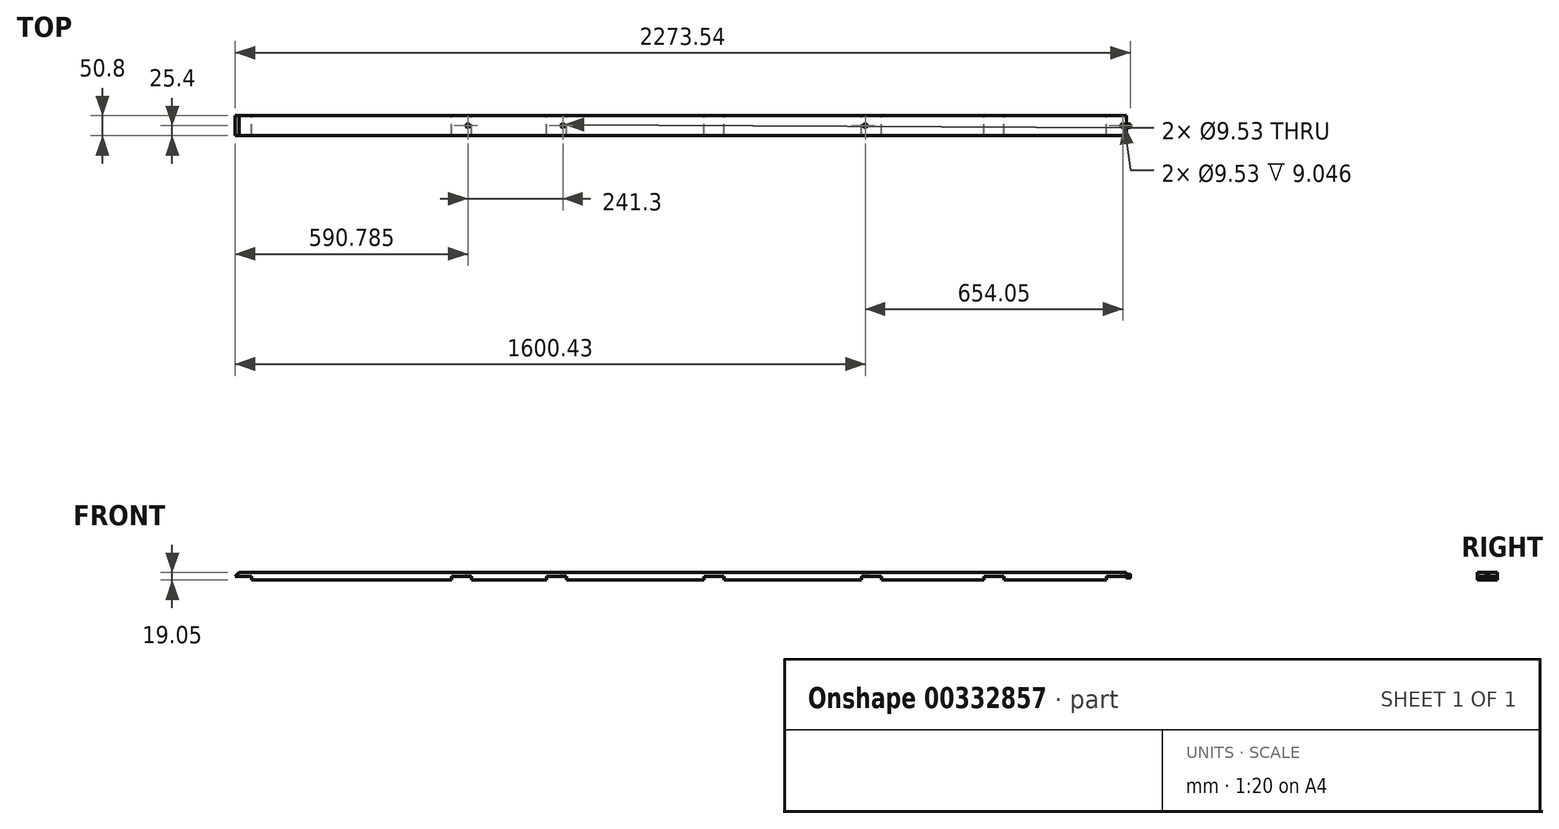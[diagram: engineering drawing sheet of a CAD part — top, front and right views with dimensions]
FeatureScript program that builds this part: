
annotation { "Feature Type Name" : "Feature", "Feature Type Description" : "" }
export const myFeature = defineFeature(function(context is Context, id is Id, definition is map)
    precondition{}
    {
        {
            var Q0;
            Q0=qCreatedBy(makeId("Front.planeOp"),FACE);
            var sketch = newSketch(context, id + "F0", { "sketchPlane" : qUnion([Q0])});
            skLineSegment(sketch, "E0.right", {"start": v(2273.3, 9.05) * mm, "end": v(2273.3, 18.57) * mm});
            skLineSegment(sketch, "E1", {"start": v(2273.3, 18.57) * mm, "end": v(18.57, 18.57) * mm});
            skPoint(sketch, "E2.left.start.orphan", {"position": v(-798.41, -3.82) * mm});
            skLineSegment(sketch, "E3.top", {"start": v(800.1, 9.52) * mm, "end": v(850.9, 9.52) * mm});
            skLineSegment(sketch, "E3.left", {"start": v(800.1, 0) * mm, "end": v(800.1, 9.52) * mm});
            skLineSegment(sketch, "E3.right", {"start": v(850.9, -0.48) * mm, "end": v(850.9, 9.52) * mm});
            skLineSegment(sketch, "E4.trimOffspring", {"start": v(850.9, -0.48) * mm, "end": v(1200.15, -0.48) * mm});
            skLineSegment(sketch, "E5.top", {"start": v(1600.2, 9.05) * mm, "end": v(1651, 9.05) * mm});
            skLineSegment(sketch, "E5.left", {"start": v(1600.2, -0.48) * mm, "end": v(1600.2, 9.05) * mm});
            skLineSegment(sketch, "E5.right", {"start": v(1651, -0.48) * mm, "end": v(1651, 9.05) * mm});
            skLineSegment(sketch, "E6.trimOffspring", {"start": v(1651, -0.48) * mm, "end": v(1911.35, -0.48) * mm});
            skLineSegment(sketch, "E7.top", {"start": v(2222.5, 9.05) * mm, "end": v(2273.3, 9.05) * mm});
            skLineSegment(sketch, "E7.left", {"start": v(2222.5, -0.48) * mm, "end": v(2222.5, 9.05) * mm});
            skPoint(sketch, "E8.orphan", {"position": v(2273.3, -0.48) * mm});
            skLineSegment(sketch, "E9", {"start": v(9.29, 9.29) * mm, "end": v(18.57, 18.57) * mm});
            skLineSegment(sketch, "E10.trimOffspring", {"start": v(50.8, 0) * mm, "end": v(558.8, 0) * mm});
            skLineSegment(sketch, "E11.top", {"start": v(9.29, 9.29) * mm, "end": v(50.8, 9.29) * mm});
            skLineSegment(sketch, "E11.right", {"start": v(50.8, 0) * mm, "end": v(50.8, 9.29) * mm});
            skPoint(sketch, "E12.orphan", {"position": v(0, 0) * mm});
            skLineSegment(sketch, "E13.bottom", {"start": v(609.6, 9.52) * mm, "end": v(558.8, 9.52) * mm});
            skLineSegment(sketch, "E13.left", {"start": v(609.6, 9.52) * mm, "end": v(609.6, 0) * mm});
            skLineSegment(sketch, "E13.right", {"start": v(558.8, 9.52) * mm, "end": v(558.8, 0) * mm});
            skLineSegment(sketch, "E14.trimOffspring", {"start": v(609.6, 0) * mm, "end": v(800.1, 0) * mm});
            skLineSegment(sketch, "E15.top", {"start": v(1962.15, 9.05) * mm, "end": v(1911.35, 9.05) * mm});
            skLineSegment(sketch, "E15.left", {"start": v(1962.15, -0.48) * mm, "end": v(1962.15, 9.05) * mm});
            skLineSegment(sketch, "E15.right", {"start": v(1911.35, -0.48) * mm, "end": v(1911.35, 9.05) * mm});
            skPoint(sketch, "E15.middle", {"position": v(1936.75, -0.48) * mm});
            skLineSegment(sketch, "E16.trimOffspring", {"start": v(1936.75, -0.48) * mm, "end": v(2222.5, -0.48) * mm});
            skPoint(sketch, "E17.orphan", {"position": v(1911.35, -10) * mm});
            skPoint(sketch, "E18.orphan", {"position": v(1962.15, -10) * mm});
            skLineSegment(sketch, "E19.top", {"start": v(1250.95, 9.05) * mm, "end": v(1200.15, 9.05) * mm});
            skLineSegment(sketch, "E19.left", {"start": v(1250.95, -0.48) * mm, "end": v(1250.95, 9.05) * mm});
            skLineSegment(sketch, "E19.right", {"start": v(1200.15, -0.48) * mm, "end": v(1200.15, 9.05) * mm});
            skPoint(sketch, "E19.middle", {"position": v(1225.55, -0.48) * mm});
            skPoint(sketch, "E19.bottom.end.orphan", {"position": v(1200.15, -10) * mm});
            skLineSegment(sketch, "E20.trimOffspring", {"start": v(1250.95, -0.48) * mm, "end": v(1600.2, -0.48) * mm});
            skPoint(sketch, "E21.orphan", {"position": v(1250.95, -10) * mm});
            skSolve(sketch);
        }
        {
            var Q0;
            Q0 = qSketchRegion(id + "F0", true);
            extrude(context, id + "F1", {"entities" : qUnion([Q0]), "depth" : 50.8 * mm});
        }
        {
            var Q0;
            Q0=qCreatedBy(makeId("Right.planeOp"),FACE);
            cPlane(context, id + "F2", {"entities" : qUnion([Q0]), "cplaneType" : CPlaneType.OFFSET, "offset" : 2273.3 * mm, "width" : 152.4 * mm, "height" : 152.4 * mm});
        }
        {
            var Q0;
            Q0=qCreatedBy(id+"F2.planeOp",FACE);
            var sketch = newSketch(context, id + "F3", { "sketchPlane" : qUnion([Q0])});
            skCircle(sketch, "E22", {"center": v(-25.4, 9.52) * mm, "radius": 4.76 * mm});
            skSolve(sketch);
        }
        {
            var Q0;
            Q0 = qSketchRegion(id + "F3", true);
            extrude(context, id + "F4", {"entities" : qUnion([Q0]), "operationType" : NewBodyOperationType.ADD, "depth" : 9.52 * mm});
        }
        {
            var Q0;
            Q0=qCreatedBy(makeId("Top.planeOp"),FACE);
            cPlane(context, id + "F5", {"entities" : qUnion([Q0]), "cplaneType" : CPlaneType.OFFSET, "offset" : 9.52 * mm, "width" : 152.4 * mm, "height" : 152.4 * mm});
        }
        {
            var Q0;
            Q0=qCreatedBy(id+"F5.planeOp",FACE);
            var sketch = newSketch(context, id + "F6", { "sketchPlane" : qUnion([Q0])});
            skCircle(sketch, "E23", {"center": v(841.37, -25.4) * mm, "radius": 4.76 * mm});
            skCircle(sketch, "E24", {"center": v(1609.72, -25.4) * mm, "radius": 4.76 * mm});
            skPoint(sketch, "E25.center.orphan", {"position": v(1609.72, -243.48) * mm});
            skCircle(sketch, "E26", {"center": v(2263.78, -25.4) * mm, "radius": 4.76 * mm});
            skCircle(sketch, "E27", {"center": v(600.07, -25.4) * mm, "radius": 4.76 * mm});
            skSolve(sketch);
        }
        {
            var Q0;
            Q0 = qSketchRegion(id + "F6", true);
            extrude(context, id + "F7", {"entities" : qUnion([Q0]), "operationType" : NewBodyOperationType.REMOVE, "depth" : 19.05 * mm, "offsetDistance" : 25.4 * mm});
        }
    });
